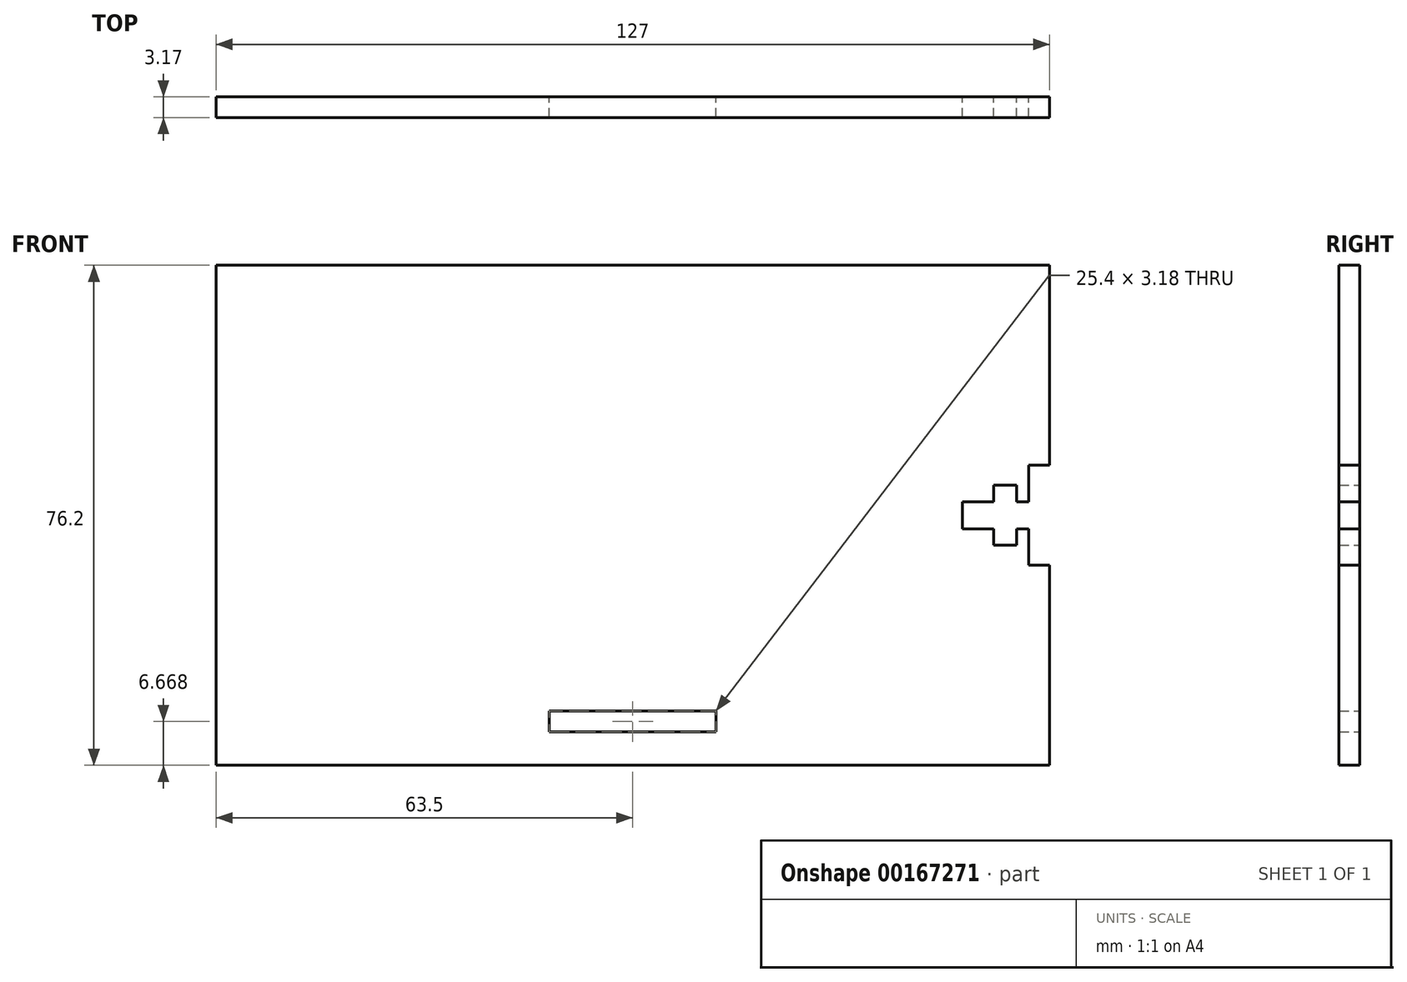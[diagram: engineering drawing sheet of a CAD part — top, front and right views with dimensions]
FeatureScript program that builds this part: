
annotation { "Feature Type Name" : "Feature", "Feature Type Description" : "" }
export const myFeature = defineFeature(function(context is Context, id is Id, definition is map)
    precondition{}
    {
        {
            var Q0;
            Q0=qCreatedBy(makeId("Front.planeOp"),FACE);
            var sketch = newSketch(context, id + "F0", { "sketchPlane" : qUnion([Q0])});
            skLineSegment(sketch, "E0.bottom", {"start": v(63.5, -38.1) * mm, "end": v(-63.5, -38.1) * mm});
            skLineSegment(sketch, "E0.top", {"start": v(63.5, 38.1) * mm, "end": v(-63.5, 38.1) * mm});
            skLineSegment(sketch, "E0.left", {"start": v(63.5, -38.1) * mm, "end": v(63.5, -7.62) * mm});
            skLineSegment(sketch, "E0.right", {"start": v(-63.5, -38.1) * mm, "end": v(-63.5, 38.1) * mm});
            skLineSegment(sketch, "E1.bottom", {"start": v(60.33, 7.62) * mm, "end": v(63.5, 7.62) * mm});
            skLineSegment(sketch, "E1.top", {"start": v(60.33, -7.62) * mm, "end": v(63.5, -7.62) * mm});
            skLineSegment(sketch, "E1.left", {"start": v(60.33, 7.62) * mm, "end": v(60.33, 2.08) * mm});
            skLineSegment(sketch, "E2.bottom", {"start": v(50.16, 2.08) * mm, "end": v(54.94, 2.08) * mm});
            skLineSegment(sketch, "E2.top", {"start": v(50.16, -2.08) * mm, "end": v(54.94, -2.08) * mm});
            skLineSegment(sketch, "E2.left", {"start": v(50.16, 2.08) * mm, "end": v(50.16, -2.08) * mm});
            skLineSegment(sketch, "E3.bottom", {"start": v(58.42, 4.57) * mm, "end": v(54.94, 4.57) * mm});
            skLineSegment(sketch, "E3.top", {"start": v(58.42, -4.57) * mm, "end": v(54.94, -4.57) * mm});
            skLineSegment(sketch, "E3.left", {"start": v(58.42, 4.57) * mm, "end": v(58.42, 2.08) * mm});
            skLineSegment(sketch, "E3.right", {"start": v(54.94, 4.57) * mm, "end": v(54.94, 2.08) * mm});
            skLineSegment(sketch, "E4.trimOffspring", {"start": v(54.94, -2.08) * mm, "end": v(54.94, -4.57) * mm});
            skLineSegment(sketch, "E5.trimOffspring", {"start": v(58.42, -2.08) * mm, "end": v(58.42, -4.57) * mm});
            skLineSegment(sketch, "E6.trimOffspring", {"start": v(60.33, -2.08) * mm, "end": v(60.33, -7.62) * mm});
            skLineSegment(sketch, "E7.trimOffspring", {"start": v(63.5, 7.62) * mm, "end": v(63.5, 38.1) * mm});
            skLineSegment(sketch, "E8.trimOffspring", {"start": v(58.42, -2.08) * mm, "end": v(60.33, -2.08) * mm});
            skLineSegment(sketch, "E9.trimOffspring", {"start": v(58.42, 2.08) * mm, "end": v(60.33, 2.08) * mm});
            skLineSegment(sketch, "E10.bottom", {"start": v(12.7, -33.02) * mm, "end": v(-12.7, -33.02) * mm});
            skLineSegment(sketch, "E10.top", {"start": v(12.7, -29.84) * mm, "end": v(-12.7, -29.84) * mm});
            skLineSegment(sketch, "E10.left", {"start": v(12.7, -33.02) * mm, "end": v(12.7, -29.84) * mm});
            skLineSegment(sketch, "E10.right", {"start": v(-12.7, -33.02) * mm, "end": v(-12.7, -29.84) * mm});
            skLineSegment(sketch, "E11", {"start": v(60.33, -2.08) * mm, "end": v(60.33, 2.08) * mm});
            skSolve(sketch);
        }
        {
            var Q0;
            Q0=makeQuery(id+"F0.imprint","IMPRINT",FACE,{"disambiguationData":[TD([[makeQuery(id+"F0.imprint","IMPRINT",EDGE,{"derivedFrom":sQuery(id+"F0.wireOp",EDGE,"E0.top")}),1.0]])]});
            extrude(context, id + "F1", {"entities" : qUnion([Q0]), "depth" : 3.17 * mm});
        }
    });
